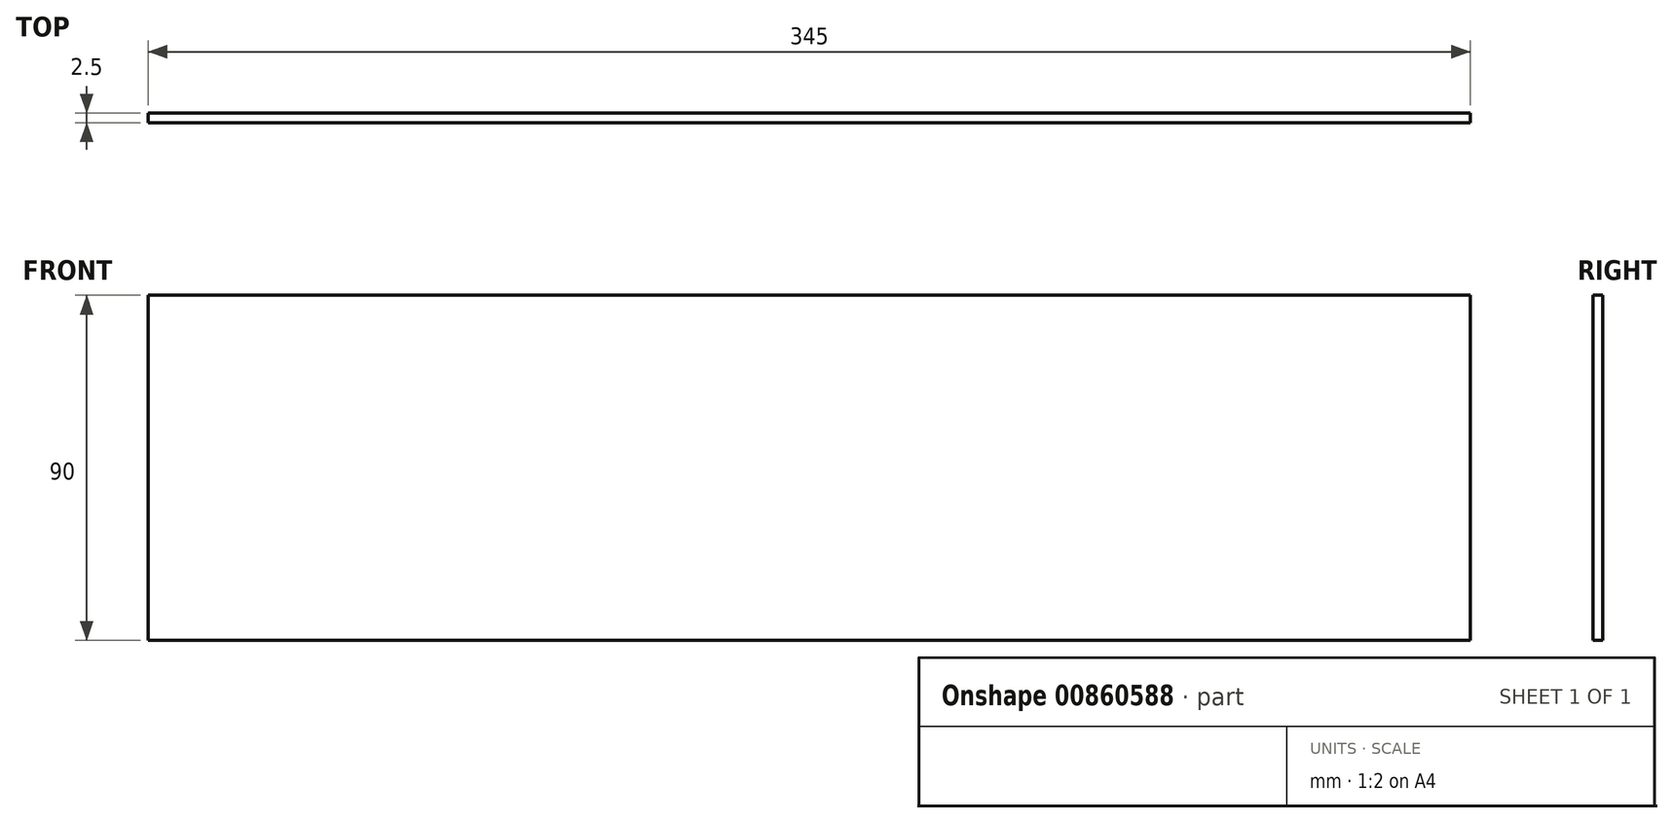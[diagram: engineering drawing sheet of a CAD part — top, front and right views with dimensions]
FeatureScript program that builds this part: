
annotation { "Feature Type Name" : "Feature", "Feature Type Description" : "" }
export const myFeature = defineFeature(function(context is Context, id is Id, definition is map)
    precondition{}
    {
        {
            var Q0;
            Q0=qCreatedBy(makeId("Front.planeOp"),FACE);
            var sketch = newSketch(context, id + "F0", { "sketchPlane" : qUnion([Q0])});
            skLineSegment(sketch, "E0.bottom", {"start": v(172.5, 45) * mm, "end": v(-172.5, 45) * mm});
            skLineSegment(sketch, "E0.top", {"start": v(172.5, -45) * mm, "end": v(-172.5, -45) * mm});
            skLineSegment(sketch, "E0.left", {"start": v(172.5, 45) * mm, "end": v(172.5, -45) * mm});
            skLineSegment(sketch, "E0.right", {"start": v(-172.5, 45) * mm, "end": v(-172.5, -45) * mm});
            skPoint(sketch, "E0.middle", {"position": v(0, 0) * mm});
            skSolve(sketch);
        }
        {
            var Q0;
            Q0 = qSketchRegion(id + "F0", true);
            extrude(context, id + "F1", {"entities" : qUnion([Q0]), "oppositeDirection" : true, "depth" : 2.5 * mm, "offsetDistance" : 25 * mm});
        }
    });
